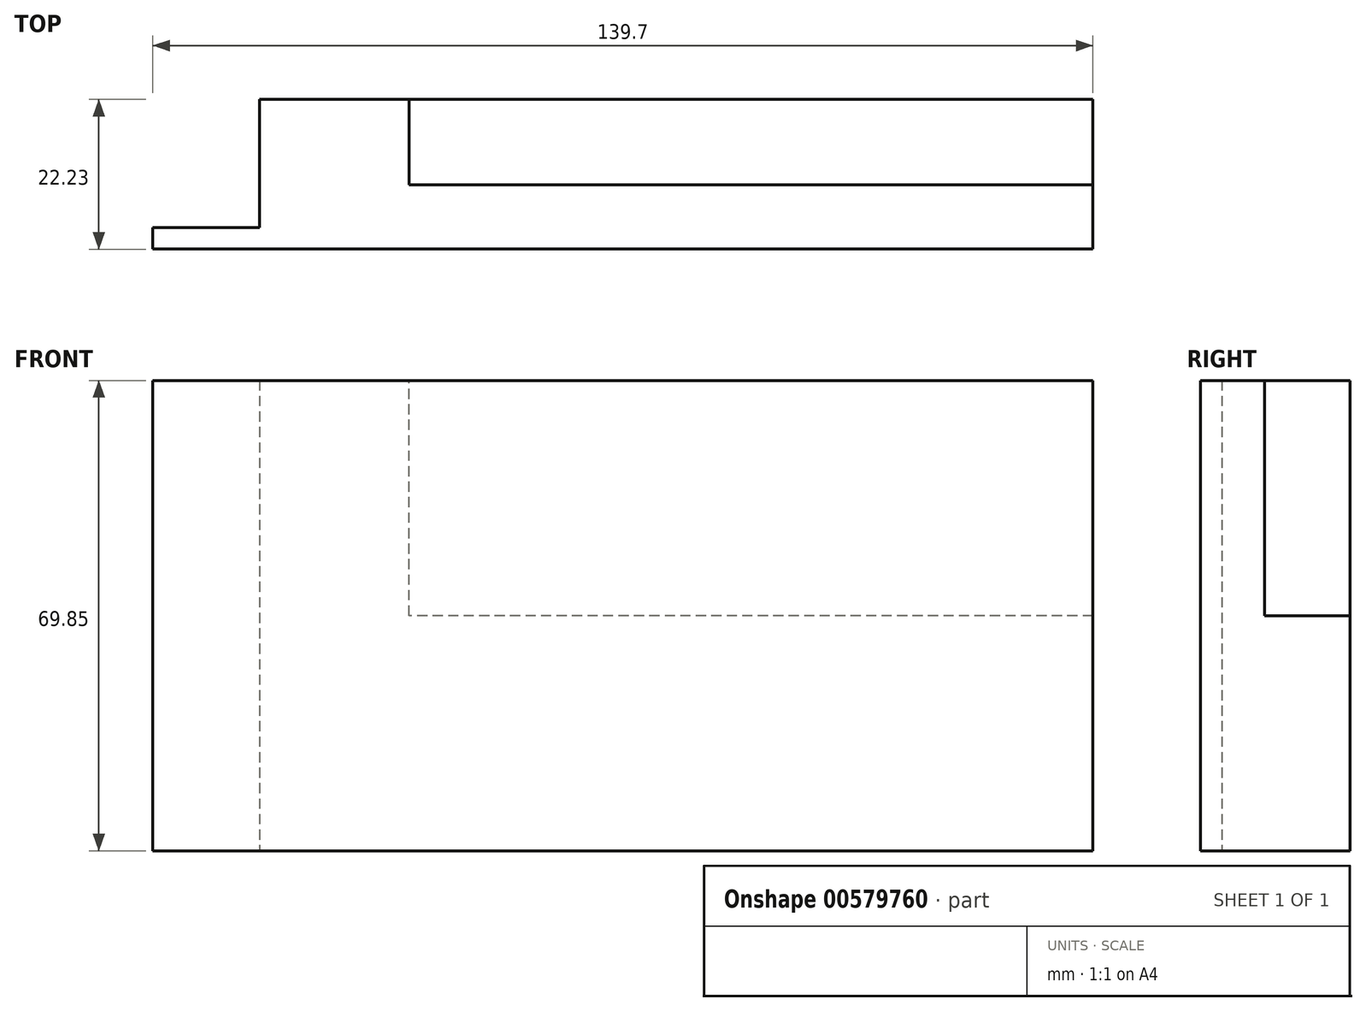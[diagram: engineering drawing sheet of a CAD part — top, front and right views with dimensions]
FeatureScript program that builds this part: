
annotation { "Feature Type Name" : "Feature", "Feature Type Description" : "" }
export const myFeature = defineFeature(function(context is Context, id is Id, definition is map)
    precondition{}
    {
        {
            var Q0;
            Q0=qCreatedBy(makeId("Front.planeOp"),FACE);
            var sketch = newSketch(context, id + "F0", { "sketchPlane" : qUnion([Q0])});
            skLineSegment(sketch, "E0", {"start": v(-63.95, 0) * mm, "end": v(-63.95, 69.85) * mm});
            skLineSegment(sketch, "E1", {"start": v(-63.95, 69.85) * mm, "end": v(75.75, 69.85) * mm});
            skLineSegment(sketch, "E2", {"start": v(75.75, 69.85) * mm, "end": v(75.75, 0) * mm});
            skLineSegment(sketch, "E3", {"start": v(75.75, 0) * mm, "end": v(-63.95, 0) * mm});
            skSolve(sketch);
        }
        {
            var Q0;
            Q0=makeQuery(id+"F0.imprint","IMPRINT",FACE,{"disambiguationData":[TD([[makeQuery(id+"F0.imprint","IMPRINT",EDGE,{"derivedFrom":sQuery(id+"F0.wireOp",EDGE,"E0")}),-1.0]])]});
            extrude(context, id + "F1", {"entities" : qUnion([Q0]), "depth" : 22.22 * mm, "offsetDistance" : 25.4 * mm});
        }
        {
            var Q0;
            Q0=qCreatedBy(makeId("Front.planeOp"),FACE);
            var sketch = newSketch(context, id + "F2", { "sketchPlane" : qUnion([Q0])});
            skLineSegment(sketch, "E4.bottom", {"start": v(75.75, 34.93) * mm, "end": v(-25.85, 34.93) * mm});
            skLineSegment(sketch, "E4.top", {"start": v(75.75, 69.85) * mm, "end": v(-25.85, 69.85) * mm});
            skLineSegment(sketch, "E4.left", {"start": v(75.75, 34.93) * mm, "end": v(75.75, 69.85) * mm});
            skLineSegment(sketch, "E4.right", {"start": v(-25.85, 34.92) * mm, "end": v(-25.85, 69.85) * mm});
            skSolve(sketch);
        }
        {
            var Q0;
            Q0=makeQuery(id+"F2.imprint","IMPRINT",FACE,{"disambiguationData":[TD([[makeQuery(id+"F2.imprint","IMPRINT",EDGE,{"derivedFrom":sQuery(id+"F2.wireOp",EDGE,"E4.bottom")}),-1.0]])]});
            extrude(context, id + "F3", {"entities" : qUnion([Q0]), "operationType" : NewBodyOperationType.REMOVE, "depth" : 12.7 * mm, "offsetDistance" : 25.4 * mm});
        }
        {
            var Q0;
            Q0=qCreatedBy(makeId("Front.planeOp"),FACE);
            var sketch = newSketch(context, id + "F4", { "sketchPlane" : qUnion([Q0])});
            skLineSegment(sketch, "E5.bottom", {"start": v(-48.07, 69.85) * mm, "end": v(-63.95, 69.85) * mm});
            skLineSegment(sketch, "E5.top", {"start": v(-48.07, 0) * mm, "end": v(-63.95, 0) * mm});
            skLineSegment(sketch, "E5.left", {"start": v(-48.07, 69.85) * mm, "end": v(-48.07, 0) * mm});
            skLineSegment(sketch, "E5.right", {"start": v(-63.95, 69.85) * mm, "end": v(-63.95, 0) * mm});
            skSolve(sketch);
        }
        {
            var Q0;
            Q0=qSketchRegion(id+"F4",true);
            extrude(context, id + "F5", {"entities" : qUnion([Q0]), "operationType" : NewBodyOperationType.REMOVE, "depth" : 19.05 * mm, "offsetDistance" : 25.4 * mm});
        }
    });
